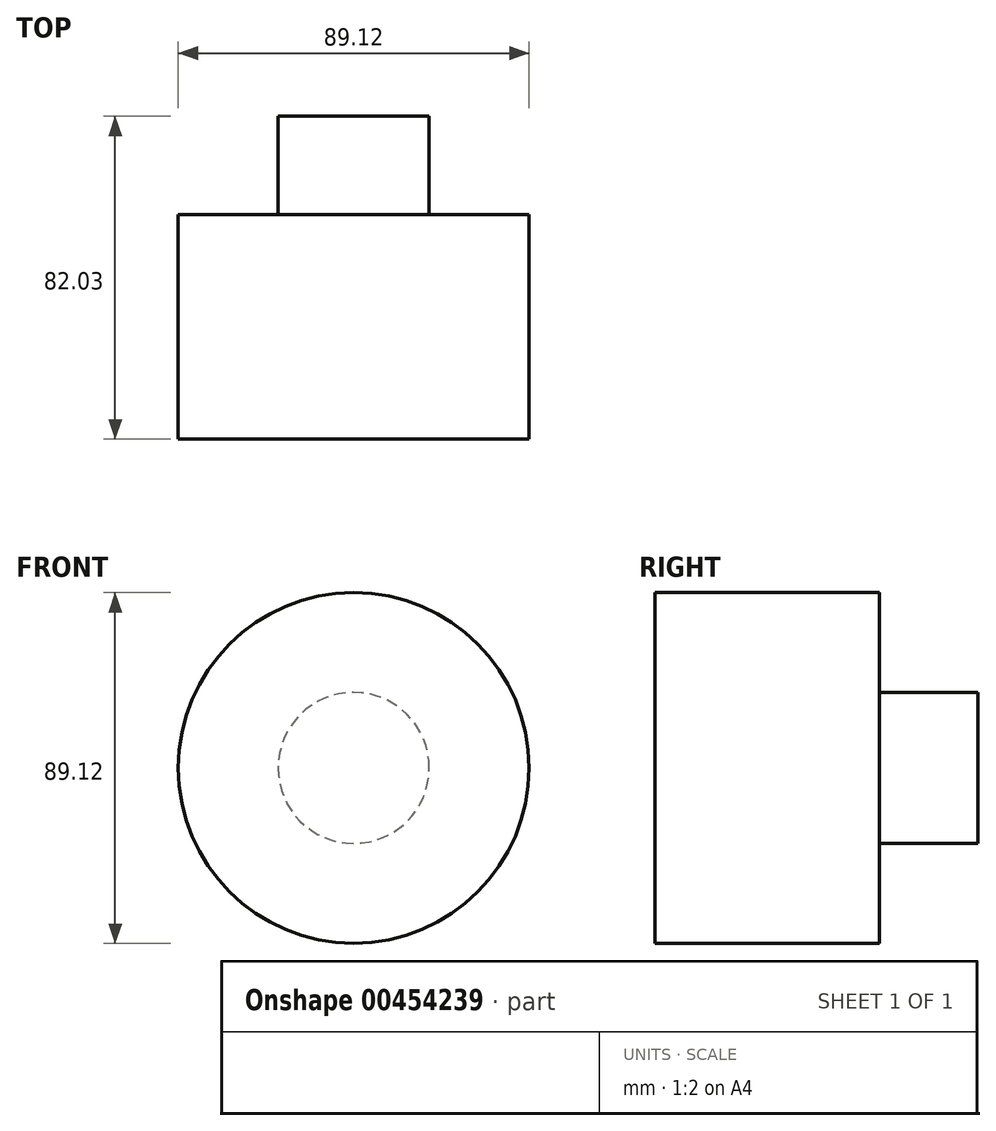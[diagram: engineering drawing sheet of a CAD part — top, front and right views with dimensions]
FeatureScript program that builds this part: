
annotation { "Feature Type Name" : "Feature", "Feature Type Description" : "" }
export const myFeature = defineFeature(function(context is Context, id is Id, definition is map)
    precondition{}
    {
        {
            var Q0;
            Q0=qCreatedBy(makeId("Top.planeOp"),FACE);
            var sketch = newSketch(context, id + "F0", { "sketchPlane" : qUnion([Q0])});
            skLineSegment(sketch, "E0.bottom", {"start": v(0, 0) * mm, "end": v(-44.56, 0) * mm});
            skLineSegment(sketch, "E0.top", {"start": v(0, 57.03) * mm, "end": v(-44.56, 57.03) * mm});
            skLineSegment(sketch, "E0.left", {"start": v(0, 0) * mm, "end": v(0, 57.03) * mm});
            skLineSegment(sketch, "E0.right", {"start": v(-44.56, 0) * mm, "end": v(-44.56, 57.03) * mm});
            skSolve(sketch);
        }
        {
            var Q0;
            Q0=makeQuery(id+"F0.imprint","IMPRINT",FACE,{"disambiguationData":[TD([[makeQuery(id+"F0.imprint","IMPRINT",EDGE,{"derivedFrom":sQuery(id+"F0.wireOp",EDGE,"E0.bottom")}),-1.0]])]});
            var Q1;
            Q1=sQuery(id+"F0.wireOp",EDGE,"E0.left");
            revolve(context, id + "F1", {"entities" : qUnion([Q0]), "axis" : qUnion([Q1]), "revolveType" : RevolveType.FULL});
        }
        {
            var Q0;
            Q0=makeQuery(id+"F1.opRevolve","SWEPT_FACE",FACE,{"disambiguationData":[OSD([sQuery(id+"F0.wireOp",EDGE,"E0.top")])]});
            var sketch = newSketch(context, id + "F2", { "sketchPlane" : qUnion([Q0])});
            skCircle(sketch, "E1", {"center": v(0, 0) * mm, "radius": 19.2 * mm});
            skSolve(sketch);
        }
        {
            var Q0;
            Q0 = qSketchRegion(id + "F2", true);
            extrude(context, id + "F3", {"entities" : qUnion([Q0]), "operationType" : NewBodyOperationType.ADD, "depth" : 25 * mm});
        }
    });
